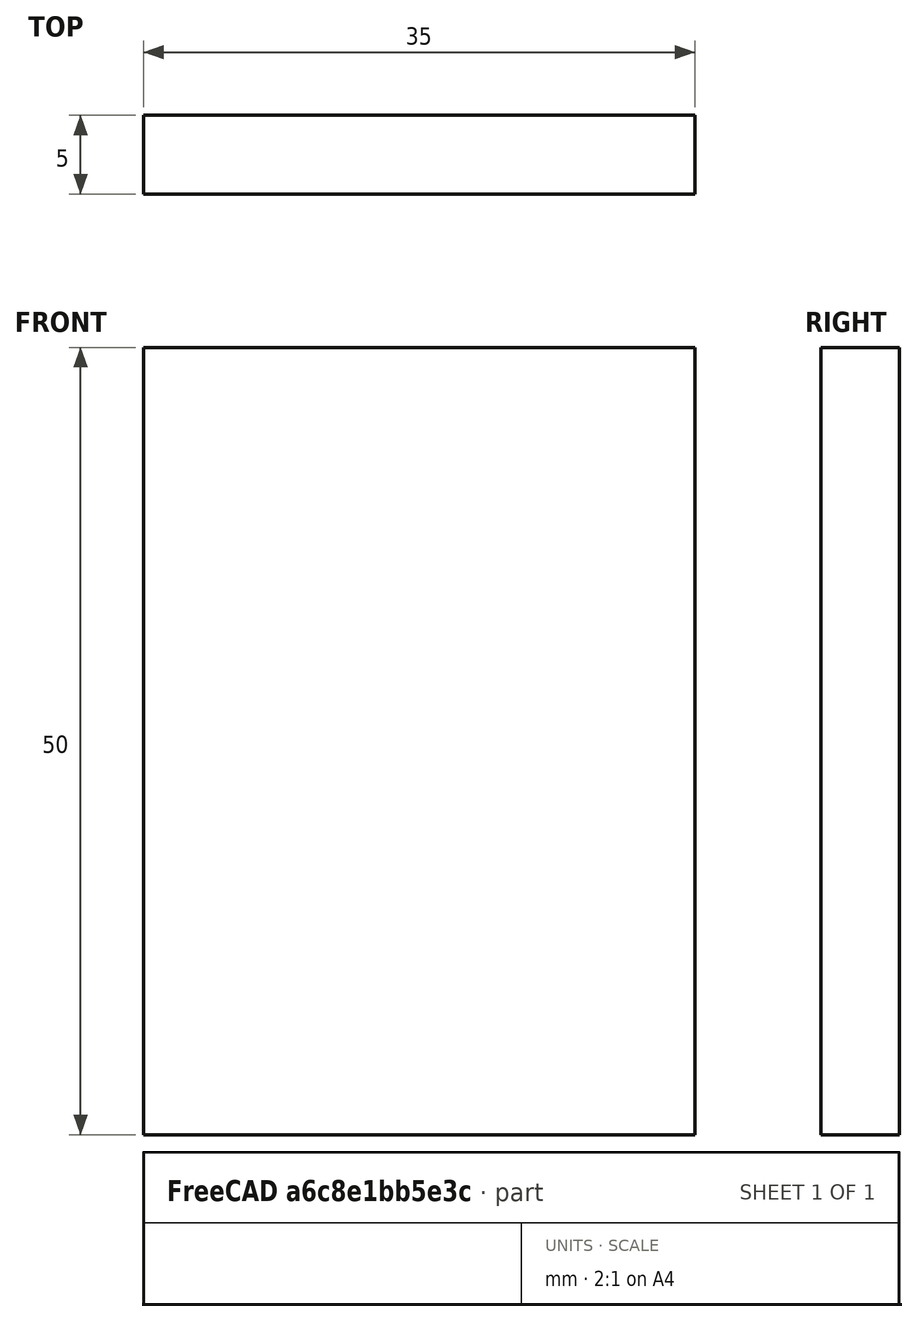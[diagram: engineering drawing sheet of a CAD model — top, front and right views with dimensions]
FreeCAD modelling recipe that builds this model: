
FCSTD DOCUMENT  (FreeCAD 0.15R4671 (Git))
Label: Flat Bar 35x5 EN10058 S235JR
License: All rights reserved
LicenseURL: http://en.wikipedia.org/wiki/All_rights_reserved
objects: Sketcher::SketchObject×1, Part::Extrusion×1
note: 2 computed .brp shape members not serialized (recipe doc carries the construction recipe); baked Part::Feature solids carry a one-line shape summary decoded from their .brp

FEATURE [Sketcher::SketchObject] Sketch
  sketch-geometry (4):
    g0: LineSegment StartX=-17.5 StartY=-2.5 StartZ=0 EndX=17.5 EndY=-2.5 EndZ=0
    g1: LineSegment StartX=17.5 StartY=-2.5 StartZ=0 EndX=17.5 EndY=2.5 EndZ=0
    g2: LineSegment StartX=17.5 StartY=2.5 StartZ=0 EndX=-17.5 EndY=2.5 EndZ=0
    g3: LineSegment StartX=-17.5 StartY=2.5 StartZ=0 EndX=-17.5 EndY=-2.5 EndZ=0
  constraints (12):
    c: Coincident(g0,g1)
    c: Coincident(g1,g2)
    c: Coincident(g2,g3)
    c: Coincident(g3,g0)
    c: Horizontal(g0)
    c: Horizontal(g2)
    c: Vertical(g1)
    c: Vertical(g3)
    c: Symmetric(g1,g2,g-2)
    c: Symmetric(g0,g1,g-1)
    c: DistanceY(g1) = 5
    c: DistanceX(g0) = 35
FEATURE [Part::Extrusion] Extrude  label="Flat Bar 35x5 EN10058 S235JR"
  Base = -> Sketch
  Dir = (0,0,50)
  Solid = true
